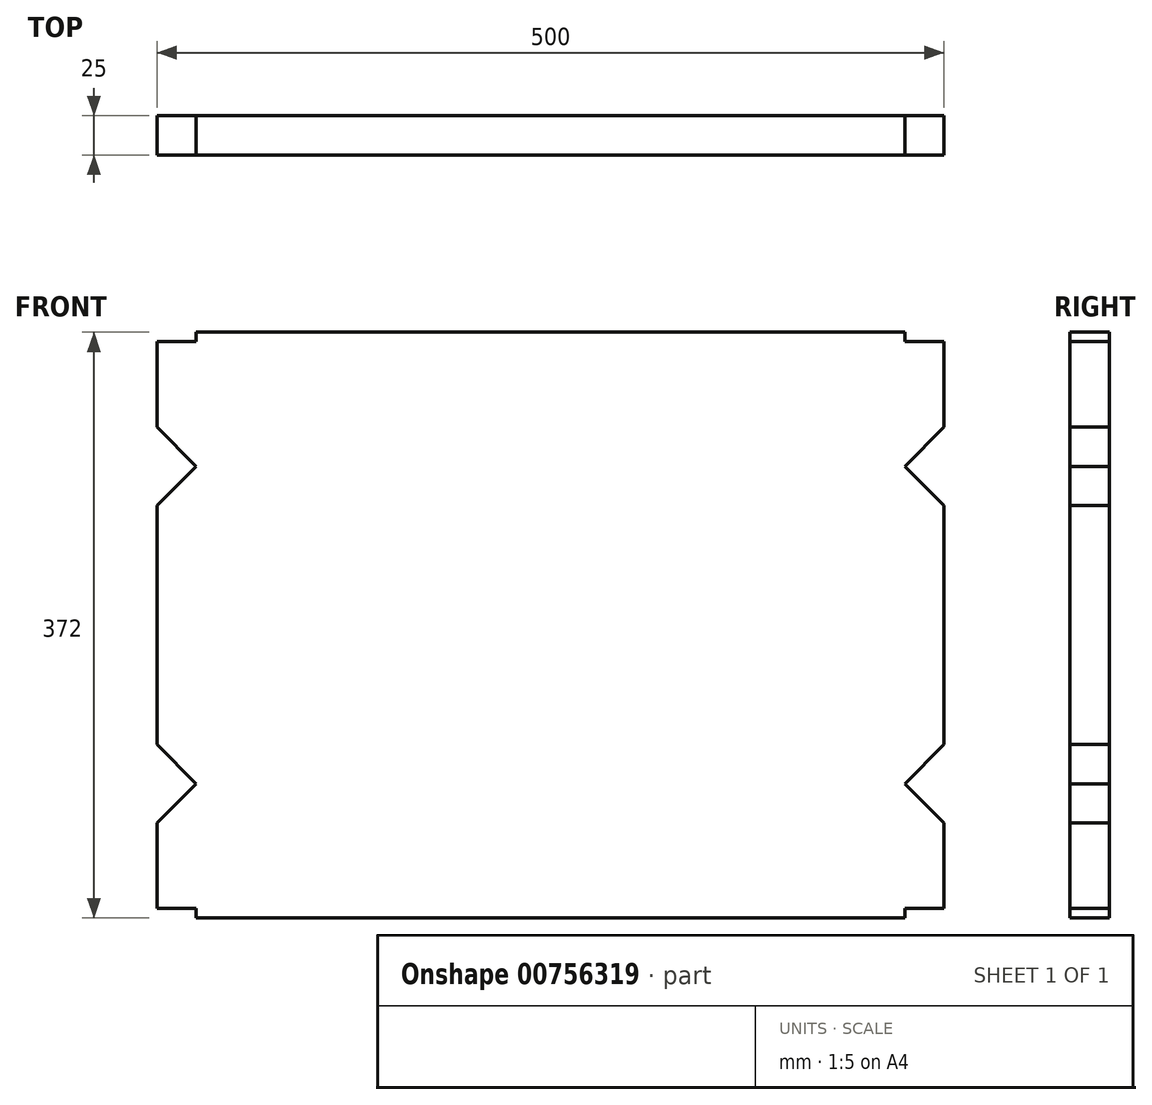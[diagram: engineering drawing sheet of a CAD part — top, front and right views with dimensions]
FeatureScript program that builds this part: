
annotation { "Feature Type Name" : "Feature", "Feature Type Description" : "" }
export const myFeature = defineFeature(function(context is Context, id is Id, definition is map)
    precondition{}
    {
        {
            var Q0;
            Q0=qCreatedBy(makeId("Front.planeOp"),FACE);
            var sketch = newSketch(context, id + "F0", { "sketchPlane" : qUnion([Q0])});
            skLineSegment(sketch, "E0.bottom", {"start": v(0, 186) * mm, "end": v(-225, 186) * mm});
            skLineSegment(sketch, "E0.right", {"start": v(-250, 180) * mm, "end": v(-250, 125.8) * mm});
            skPoint(sketch, "E0.middle", {"position": v(0, 0) * mm});
            skPoint(sketch, "E0.top.end.orphan", {"position": v(-250, -186) * mm});
            skPoint(sketch, "E0.top.start.orphan", {"position": v(250, -186) * mm});
            skPoint(sketch, "E0.left.start.orphan", {"position": v(250, 186) * mm});
            skPoint(sketch, "E1.orphan", {"position": v(250, 0) * mm});
            skLineSegment(sketch, "E2", {"start": v(-225, 186) * mm, "end": v(-225, 180) * mm});
            skLineSegment(sketch, "E3", {"start": v(-225, 180) * mm, "end": v(-250, 180) * mm});
            skPoint(sketch, "E4.orphan", {"position": v(-250, 186) * mm});
            skPoint(sketch, "E5", {"position": v(-225, 100.8) * mm});
            skLineSegment(sketch, "E6", {"start": v(-225, 100.8) * mm, "end": v(-250, 125.8) * mm});
            skLineSegment(sketch, "E7", {"start": v(-225, 100.8) * mm, "end": v(-250, 75.8) * mm});
            skPoint(sketch, "E8.right.start.orphan", {"position": v(-200, 125.8) * mm});
            skPoint(sketch, "E8.top.end.orphan", {"position": v(-200, 75.8) * mm});
            skLineSegment(sketch, "E9.trimOffspring", {"start": v(-250, 75.8) * mm, "end": v(-250, 0) * mm});
            skLineSegment(sketch, "E10.MirrorCS", {"start": v(0, 186) * mm, "end": v(225, 186) * mm});
            skLineSegment(sketch, "E11.MirrorCS", {"start": v(225, 186) * mm, "end": v(225, 180) * mm});
            skLineSegment(sketch, "E12.MirrorCS", {"start": v(225, 180) * mm, "end": v(250, 180) * mm});
            skLineSegment(sketch, "E13.MirrorCS", {"start": v(250, 180) * mm, "end": v(250, 125.8) * mm});
            skLineSegment(sketch, "E14.MirrorCS", {"start": v(225, 100.8) * mm, "end": v(250, 125.8) * mm});
            skLineSegment(sketch, "E15.MirrorCS", {"start": v(225, 100.8) * mm, "end": v(250, 75.8) * mm});
            skLineSegment(sketch, "E16.MirrorCS", {"start": v(250, 75.8) * mm, "end": v(250, 0) * mm});
            skLineSegment(sketch, "E17.MirrorCS", {"start": v(-250, -75.8) * mm, "end": v(-250, 0) * mm});
            skLineSegment(sketch, "E18.MirrorCS", {"start": v(-225, -100.8) * mm, "end": v(-250, -75.8) * mm});
            skLineSegment(sketch, "E19.MirrorCS", {"start": v(-225, -100.8) * mm, "end": v(-250, -125.8) * mm});
            skLineSegment(sketch, "E20.MirrorCS", {"start": v(-250, -180) * mm, "end": v(-250, -125.8) * mm});
            skLineSegment(sketch, "E21.MirrorCS", {"start": v(-225, -180) * mm, "end": v(-250, -180) * mm});
            skLineSegment(sketch, "E22.MirrorCS", {"start": v(-225, -186) * mm, "end": v(-225, -180) * mm});
            skLineSegment(sketch, "E23.MirrorCS", {"start": v(0, -186) * mm, "end": v(-225, -186) * mm});
            skLineSegment(sketch, "E24.MirrorCS", {"start": v(250, -75.8) * mm, "end": v(250, 0) * mm});
            skLineSegment(sketch, "E25.MirrorCS", {"start": v(225, -100.8) * mm, "end": v(250, -75.8) * mm});
            skLineSegment(sketch, "E26.MirrorCS", {"start": v(225, -100.8) * mm, "end": v(250, -125.8) * mm});
            skLineSegment(sketch, "E27.MirrorCS", {"start": v(250, -180) * mm, "end": v(250, -125.8) * mm});
            skLineSegment(sketch, "E28.MirrorCS", {"start": v(225, -180) * mm, "end": v(250, -180) * mm});
            skLineSegment(sketch, "E29.MirrorCS", {"start": v(0, -186) * mm, "end": v(225, -186) * mm});
            skLineSegment(sketch, "E30.MirrorCS", {"start": v(225, -186) * mm, "end": v(225, -180) * mm});
            skSolve(sketch);
        }
        {
            var Q0;
            Q0=makeQuery(id+"F0.imprint","IMPRINT",FACE,{"disambiguationData":[TD([[makeQuery(id+"F0.imprint","IMPRINT",EDGE,{"derivedFrom":sQuery(id+"F0.wireOp",EDGE,"E0.bottom")}),1.0]])]});
            extrude(context, id + "F1", {"entities" : qUnion([Q0]), "depth" : 25 * mm, "offsetDistance" : 25 * mm});
        }
    });
